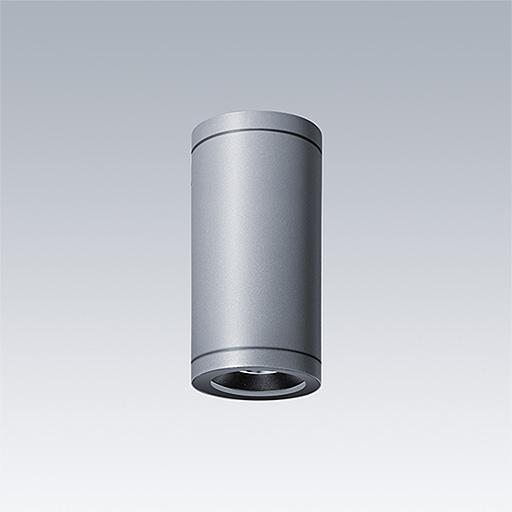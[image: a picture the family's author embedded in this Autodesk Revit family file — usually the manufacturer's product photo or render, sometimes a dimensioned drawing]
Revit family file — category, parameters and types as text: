
# Revit family: Thorn CESAR AMP CEILING
name_source: partatom
category: Lighting Fixtures
units: mm (PartAtom-declared; Revit-internal decimal feet)

## family parameters
Cut with Voids When Loaded = Yes
Host = Face
Light Source = Yes
Maintain Annotation Orientation = No
Part Type = Normal
Room Calculation Point = Yes
Round Connector Dimension = Use Diameter
Shared = No

## types (60) — shared parameters
Assembly Code = Pr_70_70_48_17
Color Filter = 16777215
Description = Outdoor Downlights
Dimming Lamp Color Temperature Shift = <None>
Emit Shape Visible in Rendering = No
Export Type to IFC As = IfcLightFixtureType
Lamp = LED
Manufacturer = Thorn Lighting
Power Factor = 1
Tilt Angle = -90.00°
Type IFC Predefined Type = DIRECTIONSOURCE
URL = https://www.thornlighting.com
zero-valued in all types: Default Elevation

## per-type parameters (varying)
| type | Apparent Load | E | Emit from Circle Diameter | Housing L | Housing M | Housing S | Luminaire Height | Luminaire Length | Luminaire Width | Material Housing | Model | Photometric Web File | R | Type Image |
| CESAR AMP S CEI 1L927WB HF ANT | 9 VA | 9 mm  [stored 0.0295276 ft] | 72 mm  [stored 0.23622 ft] | No | No | Yes | 165 mm | 90 mm  [stored 0.295276 ft] | 90 mm  [stored 0.295276 ft] | Thorn-Aluminium-RAL 7016-Anthracite Grey | 96700061 | 96700061_(STD).IES | 36 mm  [stored 0.11811 ft] | TLG_CESA_F_AMP_CEI_WB_ANT.jpg |
| CESAR AMP S CEI 1L927WB HF BK | 9 VA | 9 mm  [stored 0.0295276 ft] | 72 mm  [stored 0.23622 ft] | No | No | Yes | 165 mm | 90 mm  [stored 0.295276 ft] | 90 mm  [stored 0.295276 ft] | Thorn-Aluminium-RAL 9005-Jet Black | 96700059 | 96700059_(STD).IES | 36 mm  [stored 0.11811 ft] | TLG_CESA_F_AMP_CEI_WB_BK.jpg |
| CESAR AMP S CEI 1L927WB HF GY | 9 VA | 9 mm  [stored 0.0295276 ft] | 72 mm  [stored 0.23622 ft] | No | No | Yes | 165 mm | 90 mm  [stored 0.295276 ft] | 90 mm  [stored 0.295276 ft] | Thorn-Aluminium-RAL 9006-White Aluminium | 96700060 | 96700060_(STD).IES | 36 mm  [stored 0.11811 ft] | TLG_CESA_F_AMP_CEI_WB_GY.jpg |
| CESAR AMP S CEI 1L927WB HF WH | 9 VA | 9 mm  [stored 0.0295276 ft] | 72 mm  [stored 0.23622 ft] | No | No | Yes | 165 mm | 90 mm  [stored 0.295276 ft] | 90 mm  [stored 0.295276 ft] | Thorn-Aluminium-RAL 9016-Traffic White | 96700058 | 96700058_(STD).IES | 36 mm  [stored 0.11811 ft] | TLG_CESA_F_AMP_CEI_WB_WH.jpg |
| CESAR AMP S CEI 1L927WB RD ANT | 9 VA | 9 mm  [stored 0.0295276 ft] | 72 mm  [stored 0.23622 ft] | No | No | Yes | 165 mm | 90 mm  [stored 0.295276 ft] | 90 mm  [stored 0.295276 ft] | Thorn-Aluminium-RAL 7016-Anthracite Grey | 96701213 | 96701213_(STD).IES | 36 mm  [stored 0.11811 ft] | TLG_CESA_F_AMP_CEI_WB_ANT_DarkSkyApproved.jpg |
| CESAR AMP S CEI 1L927WB RD BK | 9 VA | 9 mm  [stored 0.0295276 ft] | 72 mm  [stored 0.23622 ft] | No | No | Yes | 165 mm | 90 mm  [stored 0.295276 ft] | 90 mm  [stored 0.295276 ft] | Thorn-Aluminium-RAL 9005-Jet Black | 96701211 | 96701211_(STD).IES | 36 mm  [stored 0.11811 ft] | TLG_CESA_F_AMP_CEI_WB_BK.jpg |
| CESAR AMP S CEI 1L927WB RD GY | 9 VA | 9 mm  [stored 0.0295276 ft] | 72 mm  [stored 0.23622 ft] | No | No | Yes | 165 mm | 90 mm  [stored 0.295276 ft] | 90 mm  [stored 0.295276 ft] | Thorn-Aluminium-RAL 9006-White Aluminium | 96701212 | 96701212_(STD).IES | 36 mm  [stored 0.11811 ft] | TLG_CESA_F_AMP_CEI_WB_GY.jpg |
| CESAR AMP S CEI 1L927WB RD WH | 9 VA | 9 mm  [stored 0.0295276 ft] | 72 mm  [stored 0.23622 ft] | No | No | Yes | 165 mm | 90 mm  [stored 0.295276 ft] | 90 mm  [stored 0.295276 ft] | Thorn-Aluminium-RAL 9016-Traffic White | 96701210 | 96701210_(STD).IES | 36 mm  [stored 0.11811 ft] | TLG_CESA_F_AMP_CEI_WB_WH.jpg |
| CESAR AMP S CEI 1L930WB HF ANT | 9 VA | 9 mm  [stored 0.0295276 ft] | 72 mm  [stored 0.23622 ft] | No | No | Yes | 165 mm | 90 mm  [stored 0.295276 ft] | 90 mm  [stored 0.295276 ft] | Thorn-Aluminium-RAL 7016-Anthracite Grey | 96700069 | 96700069_(STD).IES | 36 mm  [stored 0.11811 ft] | TLG_CESA_F_AMP_CEI_WB_ANT.jpg |
| CESAR AMP S CEI 1L930WB HF BK | 9 VA | 9 mm  [stored 0.0295276 ft] | 72 mm  [stored 0.23622 ft] | No | No | Yes | 165 mm | 90 mm  [stored 0.295276 ft] | 90 mm  [stored 0.295276 ft] | Thorn-Aluminium-RAL 9005-Jet Black | 96700067 | 96700067_(STD).IES | 36 mm  [stored 0.11811 ft] | TLG_CESA_F_AMP_CEI_WB_BK.jpg |
| CESAR AMP S CEI 1L930WB HF GY | 9 VA | 9 mm  [stored 0.0295276 ft] | 72 mm  [stored 0.23622 ft] | No | No | Yes | 165 mm | 90 mm  [stored 0.295276 ft] | 90 mm  [stored 0.295276 ft] | Thorn-Aluminium-RAL 9006-White Aluminium | 96700068 | 96700068_(STD).IES | 36 mm  [stored 0.11811 ft] | TLG_CESA_F_AMP_CEI_WB_GY.jpg |
| CESAR AMP S CEI 1L930WB HF WH | 9 VA | 9 mm  [stored 0.0295276 ft] | 72 mm  [stored 0.23622 ft] | No | No | Yes | 165 mm | 90 mm  [stored 0.295276 ft] | 90 mm  [stored 0.295276 ft] | Thorn-Aluminium-RAL 9016-Traffic White | 96700066 | 96700066_(STD).IES | 36 mm  [stored 0.11811 ft] | TLG_CESA_F_AMP_CEI_WB_WH.jpg |
| CESAR AMP S CEI 1L930WB RD ANT | 9 VA | 9 mm  [stored 0.0295276 ft] | 72 mm  [stored 0.23622 ft] | No | No | Yes | 165 mm | 90 mm  [stored 0.295276 ft] | 90 mm  [stored 0.295276 ft] | Thorn-Aluminium-RAL 7016-Anthracite Grey | 96701221 | 96701221_(STD).IES | 36 mm  [stored 0.11811 ft] | TLG_CESA_F_AMP_CEI_WB_ANT_DarkSkyApproved.jpg |
| CESAR AMP S CEI 1L930WB RD BK | 9 VA | 9 mm  [stored 0.0295276 ft] | 72 mm  [stored 0.23622 ft] | No | No | Yes | 165 mm | 90 mm  [stored 0.295276 ft] | 90 mm  [stored 0.295276 ft] | Thorn-Aluminium-RAL 9005-Jet Black | 96701219 | 96701219_(STD).IES | 36 mm  [stored 0.11811 ft] | TLG_CESA_F_AMP_CEI_WB_BK.jpg |
| CESAR AMP S CEI 1L930WB RD GY | 9 VA | 9 mm  [stored 0.0295276 ft] | 72 mm  [stored 0.23622 ft] | No | No | Yes | 165 mm | 90 mm  [stored 0.295276 ft] | 90 mm  [stored 0.295276 ft] | Thorn-Aluminium-RAL 9006-White Aluminium | 96701220 | 96701220_(STD).IES | 36 mm  [stored 0.11811 ft] | TLG_CESA_F_AMP_CEI_WB_GY.jpg |
| CESAR AMP S CEI 1L930WB RD WH | 9 VA | 9 mm  [stored 0.0295276 ft] | 72 mm  [stored 0.23622 ft] | No | No | Yes | 165 mm | 90 mm  [stored 0.295276 ft] | 90 mm  [stored 0.295276 ft] | Thorn-Aluminium-RAL 9016-Traffic White | 96701218 | 96701218_(STD).IES | 36 mm  [stored 0.11811 ft] | TLG_CESA_F_AMP_CEI_WB_WH.jpg |
| CESAR AMP S CEI 1L940WB HF ANT | 9 VA | 9 mm  [stored 0.0295276 ft] | 72 mm  [stored 0.23622 ft] | No | No | Yes | 165 mm | 90 mm  [stored 0.295276 ft] | 90 mm  [stored 0.295276 ft] | Thorn-Aluminium-RAL 7016-Anthracite Grey | 96700065 | 96700065_(STD).IES | 36 mm  [stored 0.11811 ft] | TLG_CESA_F_AMP_CEI_WB_ANT.jpg |
| CESAR AMP S CEI 1L940WB HF BK | 9 VA | 9 mm  [stored 0.0295276 ft] | 72 mm  [stored 0.23622 ft] | No | No | Yes | 165 mm | 90 mm  [stored 0.295276 ft] | 90 mm  [stored 0.295276 ft] | Thorn-Aluminium-RAL 9005-Jet Black | 96700063 | 96700063_(STD).IES | 36 mm  [stored 0.11811 ft] | TLG_CESA_F_AMP_CEI_WB_BK.jpg |
| CESAR AMP S CEI 1L940WB HF GY | 9 VA | 9 mm  [stored 0.0295276 ft] | 72 mm  [stored 0.23622 ft] | No | No | Yes | 165 mm | 90 mm  [stored 0.295276 ft] | 90 mm  [stored 0.295276 ft] | Thorn-Aluminium-RAL 9006-White Aluminium | 96700064 | 96700064_(STD).IES | 36 mm  [stored 0.11811 ft] | TLG_CESA_F_AMP_CEI_WB_GY.jpg |
| CESAR AMP S CEI 1L940WB HF WH | 9 VA | 9 mm  [stored 0.0295276 ft] | 72 mm  [stored 0.23622 ft] | No | No | Yes | 165 mm | 90 mm  [stored 0.295276 ft] | 90 mm  [stored 0.295276 ft] | Thorn-Aluminium-RAL 9016-Traffic White | 96700062 | 96700062_(STD).IES | 36 mm  [stored 0.11811 ft] | TLG_CESA_F_AMP_CEI_WB_WH.jpg |
| CESAR AMP S CEI 1L940WB RD ANT | 9 VA | 9 mm  [stored 0.0295276 ft] | 72 mm  [stored 0.23622 ft] | No | No | Yes | 165 mm | 90 mm  [stored 0.295276 ft] | 90 mm  [stored 0.295276 ft] | Thorn-Aluminium-RAL 7016-Anthracite Grey | 96701217 | 96701217_(STD).IES | 36 mm  [stored 0.11811 ft] | TLG_CESA_F_AMP_CEI_WB_BK.jpg |
| CESAR AMP S CEI 1L940WB RD BK | 9 VA | 9 mm  [stored 0.0295276 ft] | 72 mm  [stored 0.23622 ft] | No | No | Yes | 165 mm | 90 mm  [stored 0.295276 ft] | 90 mm  [stored 0.295276 ft] | Thorn-Aluminium-RAL 9005-Jet Black | 96701215 | 96701215_(STD).IES | 36 mm  [stored 0.11811 ft] | TLG_CESA_F_AMP_CEI_WB_BK.jpg |
| CESAR AMP S CEI 1L940WB RD GY | 9 VA | 9 mm  [stored 0.0295276 ft] | 72 mm  [stored 0.23622 ft] | No | No | Yes | 165 mm | 90 mm  [stored 0.295276 ft] | 90 mm  [stored 0.295276 ft] | Thorn-Aluminium-RAL 9006-White Aluminium | 96701216 | 96701216_(STD).IES | 36 mm  [stored 0.11811 ft] | TLG_CESA_F_AMP_CEI_WB_GY.jpg |
| CESAR AMP S CEI 1L940WB RD WH | 9 VA | 9 mm  [stored 0.0295276 ft] | 72 mm  [stored 0.23622 ft] | No | No | Yes | 165 mm | 90 mm  [stored 0.295276 ft] | 90 mm  [stored 0.295276 ft] | Thorn-Aluminium-RAL 9016-Traffic White | 96701214 | 96701214_(STD).IES | 36 mm  [stored 0.11811 ft] | TLG_CESA_F_AMP_CEI_WB_WH.jpg |
| CESAR AMP M CEI 1L927FX HF ANT | 19 VA | 14.5 mm  [stored 0.0475722 ft] | 111 mm  [stored 0.364173 ft] | No | Yes | No | 290 mm  [stored 0.951444 ft] | 140 mm  [stored 0.459318 ft] | 140 mm  [stored 0.459318 ft] | Thorn-Aluminium-RAL 7016-Anthracite Grey | 96700097 | 96700097_(STD).IES | 55.5 mm  [stored 0.182087 ft] | TLG_CESA_F_AMP_CEI_WB_ANT.jpg |
| CESAR AMP M CEI 1L927FX HF BK | 19 VA | 14.5 mm  [stored 0.0475722 ft] | 111 mm  [stored 0.364173 ft] | No | Yes | No | 290 mm  [stored 0.951444 ft] | 140 mm  [stored 0.459318 ft] | 140 mm  [stored 0.459318 ft] | Thorn-Aluminium-RAL 9005-Jet Black | 96700095 | 96700095_(STD).IES | 55.5 mm  [stored 0.182087 ft] | TLG_CESA_F_AMP_CEI_WB_BK.jpg |
| CESAR AMP M CEI 1L927FX HF GY | 19 VA | 14.5 mm  [stored 0.0475722 ft] | 111 mm  [stored 0.364173 ft] | No | Yes | No | 290 mm  [stored 0.951444 ft] | 140 mm  [stored 0.459318 ft] | 140 mm  [stored 0.459318 ft] | Thorn-Aluminium-RAL 9006-White Aluminium | 96700096 | 96700096_(STD).IES | 55.5 mm  [stored 0.182087 ft] | TLG_CESA_F_AMP_CEI_WB_GY.jpg |
| CESAR AMP M CEI 1L927FX HF WH | 19 VA | 14.5 mm  [stored 0.0475722 ft] | 111 mm  [stored 0.364173 ft] | No | Yes | No | 290 mm  [stored 0.951444 ft] | 140 mm  [stored 0.459318 ft] | 140 mm  [stored 0.459318 ft] | Thorn-Aluminium-RAL 9016-Traffic White | 96700094 | 96700094_(STD).IES | 55.5 mm  [stored 0.182087 ft] | TLG_CESA_F_AMP_CEI_WB_WH.jpg |
| CESAR AMP M CEI 1L927FX RD ANT | 19 VA | 14.5 mm  [stored 0.0475722 ft] | 111 mm  [stored 0.364173 ft] | No | Yes | No | 290 mm  [stored 0.951444 ft] | 140 mm  [stored 0.459318 ft] | 140 mm  [stored 0.459318 ft] | Thorn-Aluminium-RAL 7016-Anthracite Grey | 96701249 | 96701249_(STD).IES | 55.5 mm  [stored 0.182087 ft] | TLG_CESA_F_AMP_CEI_WB_ANT.jpg |
| CESAR AMP M CEI 1L927FX RD BK | 19 VA | 14.5 mm  [stored 0.0475722 ft] | 111 mm  [stored 0.364173 ft] | No | Yes | No | 290 mm  [stored 0.951444 ft] | 140 mm  [stored 0.459318 ft] | 140 mm  [stored 0.459318 ft] | Thorn-Aluminium-RAL 9005-Jet Black | 96701247 | 96701247_(STD).IES | 55.5 mm  [stored 0.182087 ft] | TLG_CESA_F_AMP_CEI_WB_BK.jpg |
| CESAR AMP M CEI 1L927FX RD GY | 19 VA | 14.5 mm  [stored 0.0475722 ft] | 111 mm  [stored 0.364173 ft] | No | Yes | No | 290 mm  [stored 0.951444 ft] | 140 mm  [stored 0.459318 ft] | 140 mm  [stored 0.459318 ft] | Thorn-Aluminium-RAL 9006-White Aluminium | 96701248 | 96701248_(STD).IES | 55.5 mm  [stored 0.182087 ft] | TLG_CESA_F_AMP_CEI_WB_GY.jpg |
| CESAR AMP M CEI 1L927FX RD WH | 19 VA | 14.5 mm  [stored 0.0475722 ft] | 111 mm  [stored 0.364173 ft] | No | Yes | No | 290 mm  [stored 0.951444 ft] | 140 mm  [stored 0.459318 ft] | 140 mm  [stored 0.459318 ft] | Thorn-Aluminium-RAL 9016-Traffic White | 96701246 | 96701246_(STD).IES | 55.5 mm  [stored 0.182087 ft] | TLG_CESA_F_AMP_CEI_WB_WH.jpg |
| CESAR AMP M CEI 1L930FX HF ANT | 19 VA | 14.5 mm  [stored 0.0475722 ft] | 111 mm  [stored 0.364173 ft] | No | Yes | No | 290 mm  [stored 0.951444 ft] | 140 mm  [stored 0.459318 ft] | 140 mm  [stored 0.459318 ft] | Thorn-Aluminium-RAL 7016-Anthracite Grey | 96700105 | 96700105_(STD).IES | 55.5 mm  [stored 0.182087 ft] | TLG_CESA_F_AMP_CEI_WB_ANT.jpg |
| CESAR AMP M CEI 1L930FX HF BK | 19 VA | 14.5 mm  [stored 0.0475722 ft] | 111 mm  [stored 0.364173 ft] | No | Yes | No | 290 mm  [stored 0.951444 ft] | 140 mm  [stored 0.459318 ft] | 140 mm  [stored 0.459318 ft] | Thorn-Aluminium-RAL 9005-Jet Black | 96700103 | 96700103_(STD).IES | 55.5 mm  [stored 0.182087 ft] | TLG_CESA_F_AMP_CEI_WB_BK.jpg |
| CESAR AMP M CEI 1L930FX HF GY | 19 VA | 14.5 mm  [stored 0.0475722 ft] | 111 mm  [stored 0.364173 ft] | No | Yes | No | 290 mm  [stored 0.951444 ft] | 140 mm  [stored 0.459318 ft] | 140 mm  [stored 0.459318 ft] | Thorn-Aluminium-RAL 9006-White Aluminium | 96700104 | 96700104_(STD).IES | 55.5 mm  [stored 0.182087 ft] | TLG_CESA_F_AMP_CEI_WB_GY.jpg |
| CESAR AMP M CEI 1L930FX HF WH | 19 VA | 14.5 mm  [stored 0.0475722 ft] | 111 mm  [stored 0.364173 ft] | No | Yes | No | 290 mm  [stored 0.951444 ft] | 140 mm  [stored 0.459318 ft] | 140 mm  [stored 0.459318 ft] | Thorn-Aluminium-RAL 9016-Traffic White | 96700102 | 96700102_(STD).IES | 55.5 mm  [stored 0.182087 ft] | TLG_CESA_F_AMP_CEI_WB_WH.jpg |
| CESAR AMP M CEI 1L930FX RD ANT | 19 VA | 14.5 mm  [stored 0.0475722 ft] | 111 mm  [stored 0.364173 ft] | No | Yes | No | 290 mm  [stored 0.951444 ft] | 140 mm  [stored 0.459318 ft] | 140 mm  [stored 0.459318 ft] | Thorn-Aluminium-RAL 7016-Anthracite Grey | 96701257 | 96701257_(STD).IES | 55.5 mm  [stored 0.182087 ft] | TLG_CESA_F_AMP_CEI_WB_ANT.jpg |
| CESAR AMP M CEI 1L930FX RD BK | 19 VA | 14.5 mm  [stored 0.0475722 ft] | 111 mm  [stored 0.364173 ft] | No | Yes | No | 290 mm  [stored 0.951444 ft] | 140 mm  [stored 0.459318 ft] | 140 mm  [stored 0.459318 ft] | Thorn-Aluminium-RAL 9005-Jet Black | 96701255 | 96701255_(STD).IES | 55.5 mm  [stored 0.182087 ft] | TLG_CESA_F_AMP_CEI_WB_BK.jpg |
| CESAR AMP M CEI 1L930FX RD GY | 19 VA | 14.5 mm  [stored 0.0475722 ft] | 111 mm  [stored 0.364173 ft] | No | Yes | No | 290 mm  [stored 0.951444 ft] | 140 mm  [stored 0.459318 ft] | 140 mm  [stored 0.459318 ft] | Thorn-Aluminium-RAL 9006-White Aluminium | 96701256 | 96701256_(STD).IES | 55.5 mm  [stored 0.182087 ft] | TLG_CESA_F_AMP_CEI_WB_GY.jpg |
| CESAR AMP M CEI 1L930FX RD WH | 19 VA | 14.5 mm  [stored 0.0475722 ft] | 111 mm  [stored 0.364173 ft] | No | Yes | No | 290 mm  [stored 0.951444 ft] | 140 mm  [stored 0.459318 ft] | 140 mm  [stored 0.459318 ft] | Thorn-Aluminium-RAL 9016-Traffic White | 96701254 | 96701254_(STD).IES | 55.5 mm  [stored 0.182087 ft] | TLG_CESA_F_AMP_CEI_WB_WH.jpg |
| CESAR AMP M CEI 1L940FX HF ANT | 19 VA | 14.5 mm  [stored 0.0475722 ft] | 111 mm  [stored 0.364173 ft] | No | Yes | No | 290 mm  [stored 0.951444 ft] | 140 mm  [stored 0.459318 ft] | 140 mm  [stored 0.459318 ft] | Thorn-Aluminium-RAL 7016-Anthracite Grey | 96700101 | 96700101_(STD).IES | 55.5 mm  [stored 0.182087 ft] | TLG_CESA_F_AMP_CEI_WB_ANT.jpg |
| CESAR AMP M CEI 1L940FX HF BK | 19 VA | 14.5 mm  [stored 0.0475722 ft] | 111 mm  [stored 0.364173 ft] | No | Yes | No | 290 mm  [stored 0.951444 ft] | 140 mm  [stored 0.459318 ft] | 140 mm  [stored 0.459318 ft] | Thorn-Aluminium-RAL 9005-Jet Black | 96700099 | 96700099_(STD).IES | 55.5 mm  [stored 0.182087 ft] | TLG_CESA_F_AMP_CEI_WB_BK.jpg |
| CESAR AMP M CEI 1L940FX HF GY | 19 VA | 14.5 mm  [stored 0.0475722 ft] | 111 mm  [stored 0.364173 ft] | No | Yes | No | 290 mm  [stored 0.951444 ft] | 140 mm  [stored 0.459318 ft] | 140 mm  [stored 0.459318 ft] | Thorn-Aluminium-RAL 9006-White Aluminium | 96700100 | 96700100_(STD).IES | 55.5 mm  [stored 0.182087 ft] | TLG_CESA_F_AMP_CEI_WB_GY.jpg |
| CESAR AMP M CEI 1L940FX HF WH | 19 VA | 14.5 mm  [stored 0.0475722 ft] | 111 mm  [stored 0.364173 ft] | No | Yes | No | 290 mm  [stored 0.951444 ft] | 140 mm  [stored 0.459318 ft] | 140 mm  [stored 0.459318 ft] | Thorn-Aluminium-RAL 9016-Traffic White | 96700098 | 96700098_(STD).IES | 55.5 mm  [stored 0.182087 ft] | TLG_CESA_F_AMP_CEI_WB_WH.jpg |
| CESAR AMP M CEI 1L940FX RD ANT | 19 VA | 14.5 mm  [stored 0.0475722 ft] | 111 mm  [stored 0.364173 ft] | No | Yes | No | 290 mm  [stored 0.951444 ft] | 140 mm  [stored 0.459318 ft] | 140 mm  [stored 0.459318 ft] | Thorn-Aluminium-RAL 7016-Anthracite Grey | 96701253 | 96701253_(STD).IES | 55.5 mm  [stored 0.182087 ft] | TLG_CESA_F_AMP_CEI_WB_ANT.jpg |
| CESAR AMP M CEI 1L940FX RD BK | 19 VA | 14.5 mm  [stored 0.0475722 ft] | 111 mm  [stored 0.364173 ft] | No | Yes | No | 290 mm  [stored 0.951444 ft] | 140 mm  [stored 0.459318 ft] | 140 mm  [stored 0.459318 ft] | Thorn-Aluminium-RAL 9005-Jet Black | 96701251 | 96701251_(STD).IES | 55.5 mm  [stored 0.182087 ft] | TLG_CESA_F_AMP_CEI_WB_BK.jpg |
| CESAR AMP M CEI 1L940FX RD GY | 19 VA | 14.5 mm  [stored 0.0475722 ft] | 111 mm  [stored 0.364173 ft] | No | Yes | No | 290 mm  [stored 0.951444 ft] | 140 mm  [stored 0.459318 ft] | 140 mm  [stored 0.459318 ft] | Thorn-Aluminium-RAL 9006-White Aluminium | 96701252 | 96701252_(STD).IES | 55.5 mm  [stored 0.182087 ft] | TLG_CESA_F_AMP_CEI_WB_GY.jpg |
| CESAR AMP M CEI 1L940FX RD WH | 19 VA | 14.5 mm  [stored 0.0475722 ft] | 111 mm  [stored 0.364173 ft] | No | Yes | No | 290 mm  [stored 0.951444 ft] | 140 mm  [stored 0.459318 ft] | 140 mm  [stored 0.459318 ft] | Thorn-Aluminium-RAL 9016-Traffic White | 96701250 | 96701250_(STD).IES | 55.5 mm  [stored 0.182087 ft] | TLG_CESA_F_AMP_CEI_WB_WH.jpg |
| CESAR AMP L CEI 1L927XB HFX ANT | 34 VA | 20 mm  [stored 0.0656168 ft] | 160 mm  [stored 0.524934 ft] | Yes | No | No | 320 mm  [stored 1.04987 ft] | 200 mm  [stored 0.656168 ft] | 200 mm  [stored 0.656168 ft] | Thorn-Aluminium-RAL 7016-Anthracite Grey | 96700133 | 96700133_(STD).IES | 80 mm  [stored 0.262467 ft] | TLG_CESA_F_AMP_CEI_WB_ANT.jpg |
| CESAR AMP L CEI 1L927XB HFX BK | 34 VA | 20 mm  [stored 0.0656168 ft] | 160 mm  [stored 0.524934 ft] | Yes | No | No | 320 mm  [stored 1.04987 ft] | 200 mm  [stored 0.656168 ft] | 200 mm  [stored 0.656168 ft] | Thorn-Aluminium-RAL 9005-Jet Black | 96700131 | 96700131_(STD).IES | 80 mm  [stored 0.262467 ft] | TLG_CESA_F_AMP_CEI_WB_BK.jpg |
| CESAR AMP L CEI 1L927XB HFX GY | 34 VA | 20 mm  [stored 0.0656168 ft] | 160 mm  [stored 0.524934 ft] | Yes | No | No | 320 mm  [stored 1.04987 ft] | 200 mm  [stored 0.656168 ft] | 200 mm  [stored 0.656168 ft] | Thorn-Aluminium-RAL 9006-White Aluminium | 96700132 | 96700132_(STD).IES | 80 mm  [stored 0.262467 ft] | TLG_CESA_F_AMP_CEI_WB_GY.jpg |
| CESAR AMP L CEI 1L927XB HFX WH | 34 VA | 20 mm  [stored 0.0656168 ft] | 160 mm  [stored 0.524934 ft] | Yes | No | No | 320 mm  [stored 1.04987 ft] | 200 mm  [stored 0.656168 ft] | 200 mm  [stored 0.656168 ft] | Thorn-Aluminium-RAL 9016-Traffic White | 96700130 | 96700130_(STD).IES | 80 mm  [stored 0.262467 ft] | TLG_CESA_F_AMP_CEI_WB_WH.jpg |
| CESAR AMP L CEI 1L930XB HFX ANT | 34 VA | 20 mm  [stored 0.0656168 ft] | 160 mm  [stored 0.524934 ft] | Yes | No | No | 320 mm  [stored 1.04987 ft] | 200 mm  [stored 0.656168 ft] | 200 mm  [stored 0.656168 ft] | Thorn-Aluminium-RAL 7016-Anthracite Grey | 96700141 | 96700141_(STD).IES | 80 mm  [stored 0.262467 ft] | TLG_CESA_F_AMP_CEI_WB_ANT.jpg |
| CESAR AMP L CEI 1L930XB HFX BK | 34 VA | 20 mm  [stored 0.0656168 ft] | 160 mm  [stored 0.524934 ft] | Yes | No | No | 320 mm  [stored 1.04987 ft] | 200 mm  [stored 0.656168 ft] | 200 mm  [stored 0.656168 ft] | Thorn-Aluminium-RAL 9005-Jet Black | 96700139 | 96700139_(STD).IES | 80 mm  [stored 0.262467 ft] | TLG_CESA_F_AMP_CEI_WB_BK.jpg |
| CESAR AMP L CEI 1L930XB HFX GY | 34 VA | 20 mm  [stored 0.0656168 ft] | 160 mm  [stored 0.524934 ft] | Yes | No | No | 320 mm  [stored 1.04987 ft] | 200 mm  [stored 0.656168 ft] | 200 mm  [stored 0.656168 ft] | Thorn-Aluminium-RAL 9006-White Aluminium | 96700140 | 96700140_(STD).IES | 80 mm  [stored 0.262467 ft] | TLG_CESA_F_AMP_CEI_WB_GY.jpg |
| CESAR AMP L CEI 1L930XB HFX WH | 34 VA | 20 mm  [stored 0.0656168 ft] | 160 mm  [stored 0.524934 ft] | Yes | No | No | 320 mm  [stored 1.04987 ft] | 200 mm  [stored 0.656168 ft] | 200 mm  [stored 0.656168 ft] | Thorn-Aluminium-RAL 9016-Traffic White | 96700138 | 96700138_(STD).IES | 80 mm  [stored 0.262467 ft] | TLG_CESA_F_AMP_CEI_WB_WH.jpg |
| CESAR AMP L CEI 1L940XB HFX ANT | 34 VA | 20 mm  [stored 0.0656168 ft] | 160 mm  [stored 0.524934 ft] | Yes | No | No | 320 mm  [stored 1.04987 ft] | 200 mm  [stored 0.656168 ft] | 200 mm  [stored 0.656168 ft] | Thorn-Aluminium-RAL 7016-Anthracite Grey | 96700137 | 96700137_(STD).IES | 80 mm  [stored 0.262467 ft] | TLG_CESA_F_AMP_CEI_WB_ANT.jpg |
| CESAR AMP L CEI 1L940XB HFX BK | 34 VA | 20 mm  [stored 0.0656168 ft] | 160 mm  [stored 0.524934 ft] | Yes | No | No | 320 mm  [stored 1.04987 ft] | 200 mm  [stored 0.656168 ft] | 200 mm  [stored 0.656168 ft] | Thorn-Aluminium-RAL 9005-Jet Black | 96700135 | 96700135_(STD).IES | 80 mm  [stored 0.262467 ft] | TLG_CESA_F_AMP_CEI_WB_BK.jpg |
| CESAR AMP L CEI 1L940XB HFX GY | 34 VA | 20 mm  [stored 0.0656168 ft] | 160 mm  [stored 0.524934 ft] | Yes | No | No | 320 mm  [stored 1.04987 ft] | 200 mm  [stored 0.656168 ft] | 200 mm  [stored 0.656168 ft] | Thorn-Aluminium-RAL 9006-White Aluminium | 96700136 | 96700136_(STD).IES | 80 mm  [stored 0.262467 ft] | TLG_CESA_F_AMP_CEI_WB_GY.jpg |
| CESAR AMP L CEI 1L940XB HFX WH | 34 VA | 20 mm  [stored 0.0656168 ft] | 160 mm  [stored 0.524934 ft] | Yes | No | No | 320 mm  [stored 1.04987 ft] | 200 mm  [stored 0.656168 ft] | 200 mm  [stored 0.656168 ft] | Thorn-Aluminium-RAL 9016-Traffic White | 96700134 | 96700134_(STD).IES | 80 mm  [stored 0.262467 ft] | TLG_CESA_F_AMP_CEI_WB_WH.jpg |

note: [stored X ft] marks values corroborated as IEEE doubles in the binary element streams (Revit-internal decimal feet)

## geometry (parser evidence)
native form markers: Sweep x4
no freeform markers — native parametric forms only
